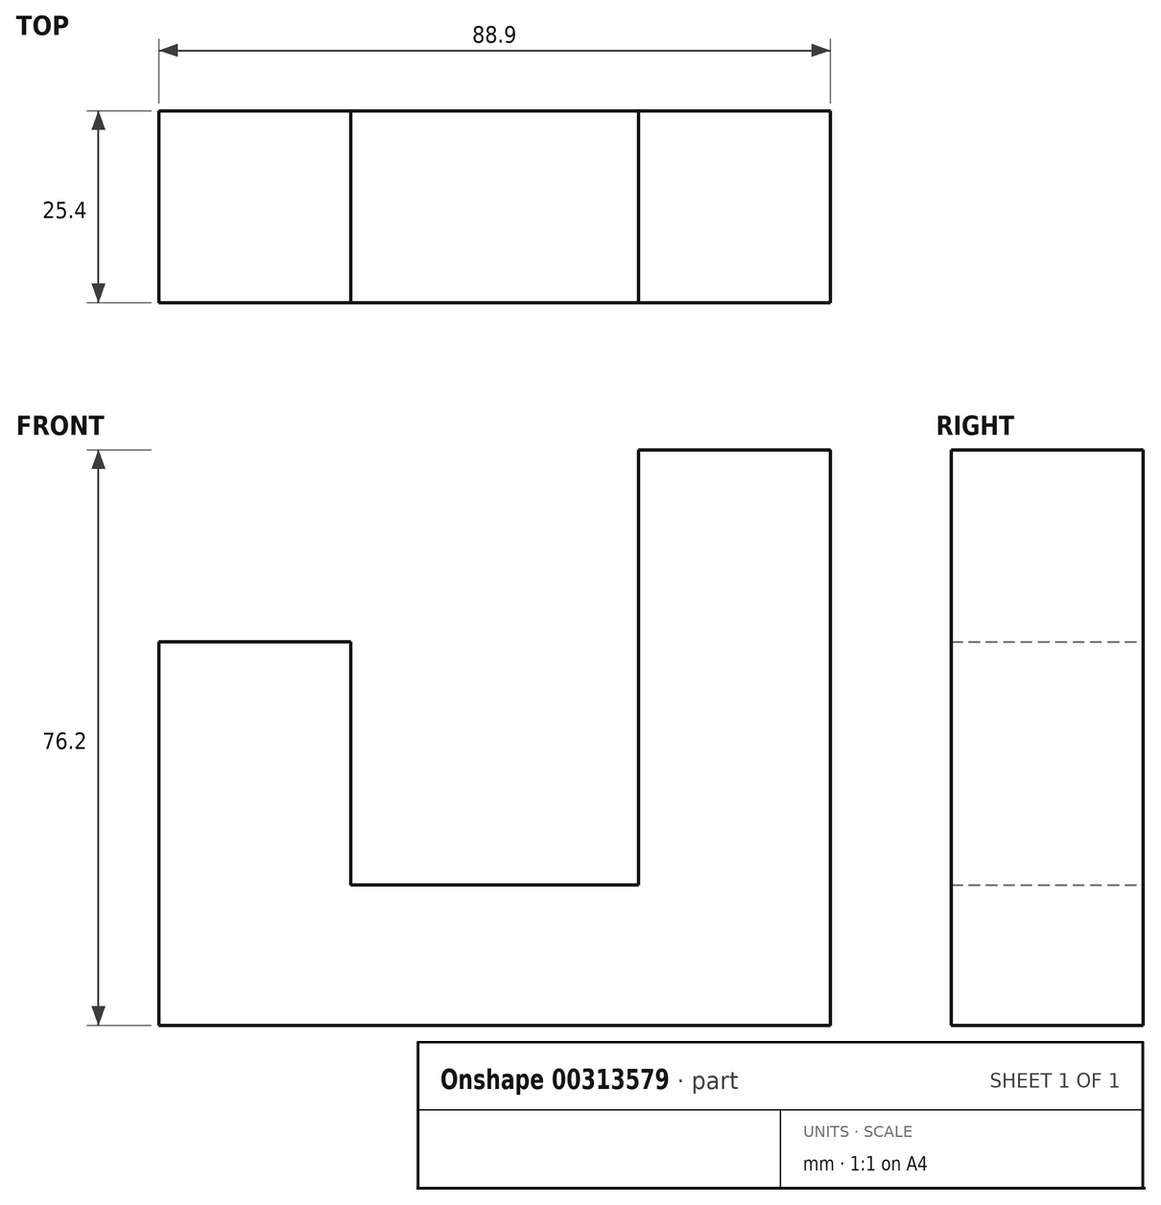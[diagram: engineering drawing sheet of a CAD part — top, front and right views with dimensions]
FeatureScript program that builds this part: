
annotation { "Feature Type Name" : "Feature", "Feature Type Description" : "" }
export const myFeature = defineFeature(function(context is Context, id is Id, definition is map)
    precondition{}
    {
        {
            var Q0;
            Q0=qCreatedBy(makeId("Front.planeOp"),FACE);
            var sketch = newSketch(context, id + "F0", { "sketchPlane" : qUnion([Q0])});
            skLineSegment(sketch, "E0", {"start": v(-27.71, -47.1) * mm, "end": v(61.19, -47.1) * mm});
            skLineSegment(sketch, "E1", {"start": v(61.19, -47.1) * mm, "end": v(61.19, 29.1) * mm});
            skLineSegment(sketch, "E2", {"start": v(61.19, 29.1) * mm, "end": v(35.79, 29.1) * mm});
            skLineSegment(sketch, "E3", {"start": v(35.79, 29.1) * mm, "end": v(35.79, -28.5) * mm});
            skLineSegment(sketch, "E4", {"start": v(35.79, -28.5) * mm, "end": v(-2.31, -28.5) * mm});
            skLineSegment(sketch, "E5", {"start": v(-2.31, -28.5) * mm, "end": v(-2.31, 3.7) * mm});
            skLineSegment(sketch, "E6", {"start": v(-2.31, 3.7) * mm, "end": v(-27.71, 3.7) * mm});
            skLineSegment(sketch, "E7", {"start": v(-27.71, 3.7) * mm, "end": v(-27.71, -47.1) * mm});
            skSolve(sketch);
        }
        {
            var Q0;
            Q0=makeQuery(id+"F0.imprint","IMPRINT",FACE,{"disambiguationData":[TD([[makeQuery(id+"F0.imprint","IMPRINT",EDGE,{"derivedFrom":sQuery(id+"F0.wireOp",EDGE,"E0")}),1.0]])]});
            extrude(context, id + "F1", {"entities" : qUnion([Q0]), "depth" : 25.4 * mm});
        }
    });
